# Revit family: Table-Teknion-CQTMR_Routes_Rectangular_Meeting_Table-R2018
name_source: partatom
category: Furniture
revit_build: Autodesk Revit 2018 (Build: 20170223_1515(x64)
units: mm (PartAtom-declared; Revit-internal decimal feet)

## family parameters
Always vertical = Yes
Cut with Voids When Loaded = No
OmniClass Number = 23.40.20.00
OmniClass Title = General Furniture and Specialties
Room Calculation Point = No
Shared = Yes
Work Plane-Based = No

## types (2) — shared parameters
Assembly Code = E2020200
Manufacturer = Teknion
Manufacturer Fax = 416.661.4586
Part Number = CQTMR
Product Documentation Link = https://assets.teknion.com
Product Line = Routes
Product Page URL = https://www.teknion.com
Series = Routes
Sustainability Data = https://www.teknion.com
URL = www.teknion.com
Unit Weight URL = http://www.teknion.com
Warranty = http://www.teknion.com

## per-type parameters (varying)
| type | Depth | Description | Model | Tube Horizontal Spacing | Width |
| 36"d x 84"w | 36.2 " | Routes Rectangular Meeting Table, 36" Depth, 84" Width | CQTMR3684 | 14.128 " | 84.2 " |
| 42"d x 96"w | 42.2 " | Routes Rectangular Meeting Table, 42" Depth, 96" Width | CQTMR4296 | 17.597 " | 96.2 " |

## geometry (parser evidence)
native form markers: Sweep x4
no freeform markers — native parametric forms only
